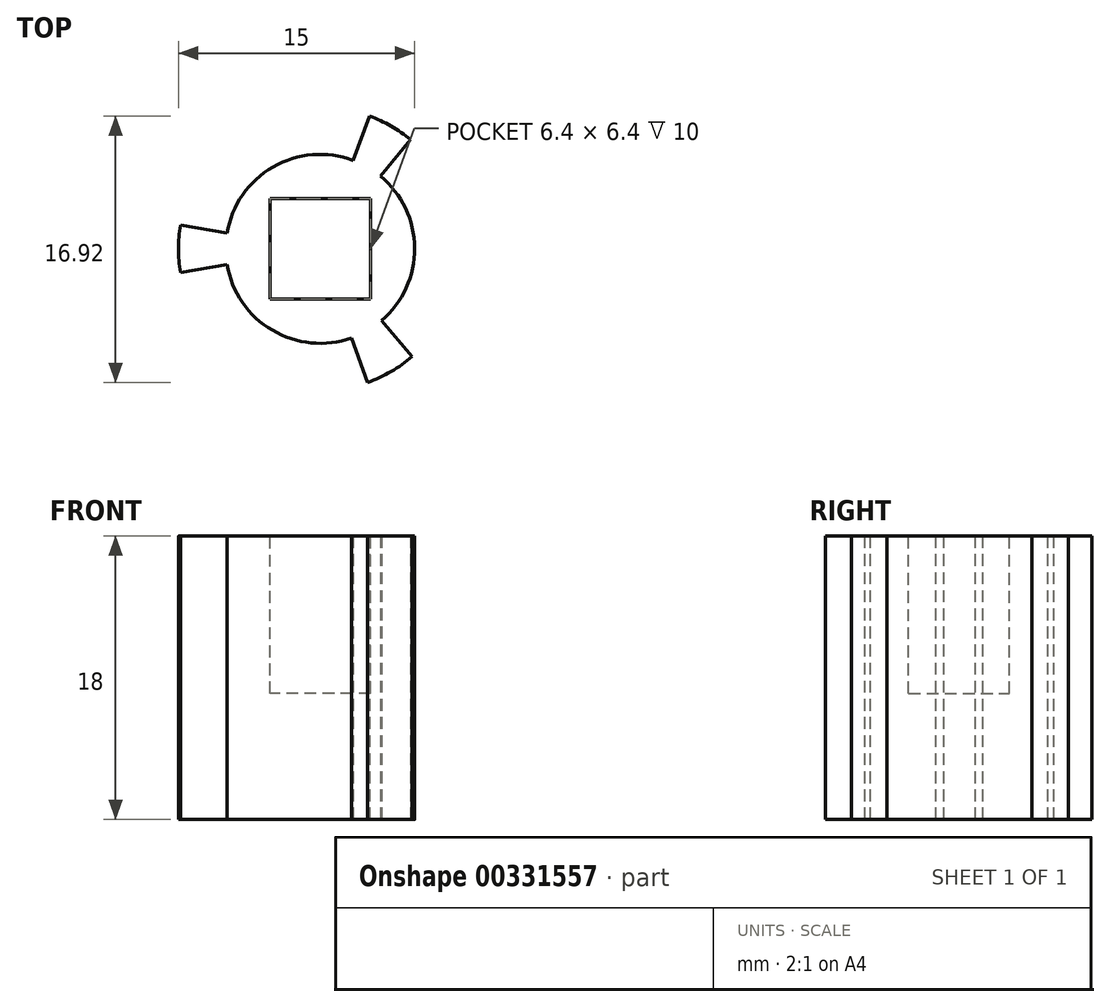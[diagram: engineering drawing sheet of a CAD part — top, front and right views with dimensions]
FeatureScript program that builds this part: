
annotation { "Feature Type Name" : "Feature", "Feature Type Description" : "" }
export const myFeature = defineFeature(function(context is Context, id is Id, definition is map)
    precondition{}
    {
        {
            var Q0;
            Q0=qCreatedBy(makeId("Top.planeOp"),FACE);
            var sketch = newSketch(context, id + "F0", { "sketchPlane" : qUnion([Q0])});
            skCircle(sketch, "E0", {"center": v(0, 0) * mm, "radius": 9 * mm});
            skCircle(sketch, "E1.cCircle", {"center": v(0, 0) * mm, "radius": 9 * mm, "construction": true});
            skLineSegment(sketch, "E1.0", {"start": v(-9, 0) * mm, "end": v(4.5, 7.8) * mm, "construction": true});
            skLineSegment(sketch, "E1.1", {"start": v(4.5, 7.8) * mm, "end": v(4.5, -7.8) * mm, "construction": true});
            skLineSegment(sketch, "E1.2", {"start": v(4.5, -7.8) * mm, "end": v(-9, 0) * mm, "construction": true});
            skCircle(sketch, "E2", {"center": v(0, 0) * mm, "radius": 6 * mm});
            skPoint(sketch, "E3", {"position": v(-8.87, 1.5) * mm});
            skPoint(sketch, "E4", {"position": v(-8.87, -1.5) * mm});
            skLineSegment(sketch, "E5", {"start": v(-8.87, 1.5) * mm, "end": v(-5.92, 1) * mm});
            skLineSegment(sketch, "E6", {"start": v(-8.87, -1.5) * mm, "end": v(-5.92, -1) * mm});
            skPoint(sketch, "E7", {"position": v(3.14, 8.43) * mm});
            skPoint(sketch, "E8", {"position": v(5.73, 6.94) * mm});
            skPoint(sketch, "E9", {"position": v(5.85, -6.84) * mm});
            skPoint(sketch, "E10", {"position": v(3, -8.49) * mm});
            skLineSegment(sketch, "E11", {"start": v(4.5, 7.8) * mm, "end": v(0, 0) * mm, "construction": true});
            skLineSegment(sketch, "E12", {"start": v(4.5, -7.8) * mm, "end": v(0, 0) * mm, "construction": true});
            skLineSegment(sketch, "E13", {"start": v(3.14, 8.43) * mm, "end": v(2.1, 5.62) * mm});
            skLineSegment(sketch, "E14", {"start": v(5.73, 6.94) * mm, "end": v(3.82, 4.63) * mm});
            skLineSegment(sketch, "E15", {"start": v(5.85, -6.84) * mm, "end": v(3.9, -4.56) * mm});
            skLineSegment(sketch, "E16", {"start": v(3, -8.49) * mm, "end": v(2, -5.66) * mm});
            skSolve(sketch);
        }
        {
            var Q0;
            {var subQ0=sQuery(id+"F0.wireOp",EDGE,"E5");Q0=makeQuery(id+"F0.imprint","IMPRINT",FACE,{"disambiguationData":[TD([[makeQuery(id+"F0.imprint","IMPRINT",EDGE,{"derivedFrom":subQ0}),-1.0]])]});}
            var Q1;
            {var subQ0=sQuery(id+"F0.wireOp",EDGE,"E2");var subQ4=makeQuery(id+"F0.imprint","INTERSECT",VERTEX,{"derivedFrom":[subQ0,sQuery(id+"F0.wireOp",EDGE,"E13")]});Q1=makeQuery(id+"F0.imprint","IMPRINT",FACE,{"disambiguationData":[TD([[makeQuery(id+"F0.imprint","IMPRINT",EDGE,{"disambiguationData":[TD([[subQ4,1.0]])],"derivedFrom":subQ0}),1.0]])]});}
            var Q2;
            {var subQ0=sQuery(id+"F0.wireOp",EDGE,"E13");Q2=makeQuery(id+"F0.imprint","IMPRINT",FACE,{"disambiguationData":[TD([[makeQuery(id+"F0.imprint","IMPRINT",EDGE,{"derivedFrom":subQ0}),1.0]])]});}
            var Q3;
            {var subQ0=sQuery(id+"F0.wireOp",EDGE,"E15");Q3=makeQuery(id+"F0.imprint","IMPRINT",FACE,{"disambiguationData":[TD([[makeQuery(id+"F0.imprint","IMPRINT",EDGE,{"derivedFrom":subQ0}),1.0]])]});}
            extrude(context, id + "F1", {"entities" : qUnion([Q0, Q1, Q2, Q3]), "depth" : 18 * mm});
        }
        {
            var Q0;
            Q0=makeQuery(id+"F1.opExtrude","CAP_FACE",FACE,{"disambiguationData":[OSD([sQuery(id+"F0.wireOp",EDGE,"E0"),sQuery(id+"F0.wireOp",EDGE,"E2"),sQuery(id+"F0.wireOp",EDGE,"E5"),sQuery(id+"F0.wireOp",EDGE,"E6"),sQuery(id+"F0.wireOp",EDGE,"E13"),sQuery(id+"F0.wireOp",EDGE,"E14"),sQuery(id+"F0.wireOp",EDGE,"E15"),sQuery(id+"F0.wireOp",EDGE,"E16")])],"isStart":false});
            var sketch = newSketch(context, id + "F2", { "sketchPlane" : qUnion([Q0])});
            skCircle(sketch, "E17.cCircle", {"center": v(0, 0) * mm, "radius": 3.2 * mm, "construction": true});
            skLineSegment(sketch, "E17.0", {"start": v(-3.2, -3.2) * mm, "end": v(-3.2, 3.2) * mm});
            skLineSegment(sketch, "E17.1", {"start": v(-3.2, 3.2) * mm, "end": v(3.2, 3.2) * mm});
            skLineSegment(sketch, "E17.2", {"start": v(3.2, 3.2) * mm, "end": v(3.2, -3.2) * mm});
            skLineSegment(sketch, "E17.3", {"start": v(3.2, -3.2) * mm, "end": v(-3.2, -3.2) * mm});
            skPoint(sketch, "E17.0.midPoint", {"position": v(-3.2, 0) * mm});
            skSolve(sketch);
        }
        {
            var Q0;
            Q0=qSketchRegion(id+"F2",true);
            extrude(context, id + "F3", {"entities" : qUnion([Q0]), "operationType" : NewBodyOperationType.REMOVE, "depth" : -10 * mm});
        }
    });
